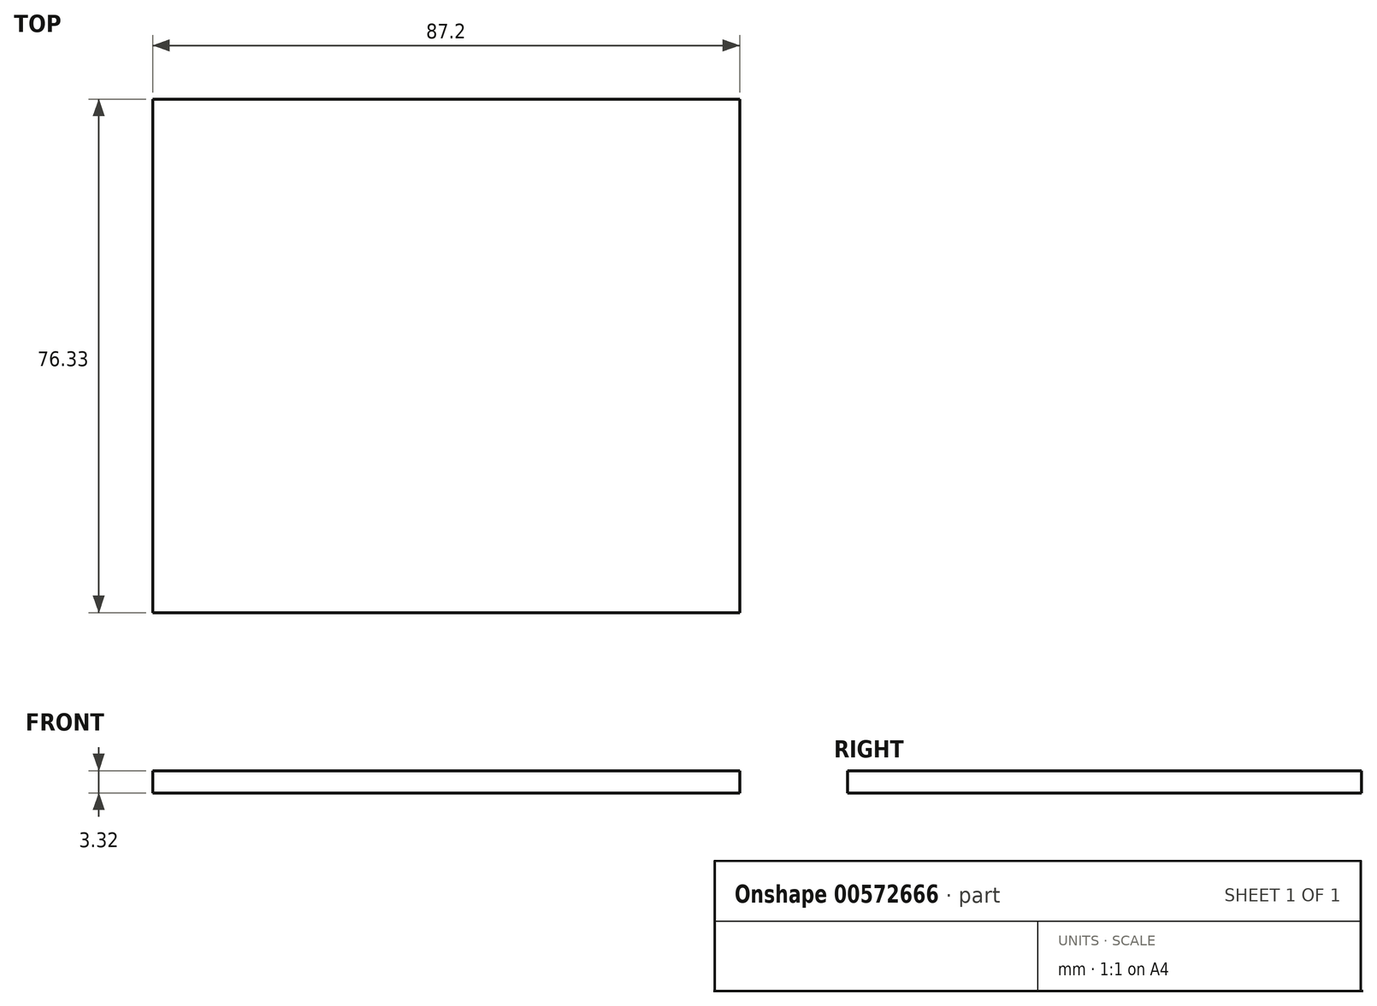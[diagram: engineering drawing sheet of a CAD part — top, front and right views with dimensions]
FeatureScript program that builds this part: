
annotation { "Feature Type Name" : "Feature", "Feature Type Description" : "" }
export const myFeature = defineFeature(function(context is Context, id is Id, definition is map)
    precondition{}
    {
        {
            var Q0;
            Q0=qCreatedBy(makeId("Top.planeOp"),FACE);
            var sketch = newSketch(context, id + "F0", { "sketchPlane" : qUnion([Q0])});
            skLineSegment(sketch, "E0.bottom", {"start": v(48.54, 44.3) * mm, "end": v(-38.66, 44.3) * mm});
            skLineSegment(sketch, "E0.top", {"start": v(48.54, -32.02) * mm, "end": v(-38.66, -32.02) * mm});
            skLineSegment(sketch, "E0.left", {"start": v(48.54, 44.3) * mm, "end": v(48.54, -32.02) * mm});
            skLineSegment(sketch, "E0.right", {"start": v(-38.66, 44.3) * mm, "end": v(-38.66, -32.02) * mm});
            skSolve(sketch);
        }
        {
            var Q0;
            Q0=makeQuery(id+"F0.imprint","IMPRINT",FACE,{"disambiguationData":[TD([[makeQuery(id+"F0.imprint","IMPRINT",EDGE,{"derivedFrom":sQuery(id+"F0.wireOp",EDGE,"E0.bottom")}),1.0]])]});
            extrude(context, id + "F1", {"entities" : qUnion([Q0]), "depth" : 3.32 * mm, "offsetDistance" : 25.4 * mm});
        }
    });
